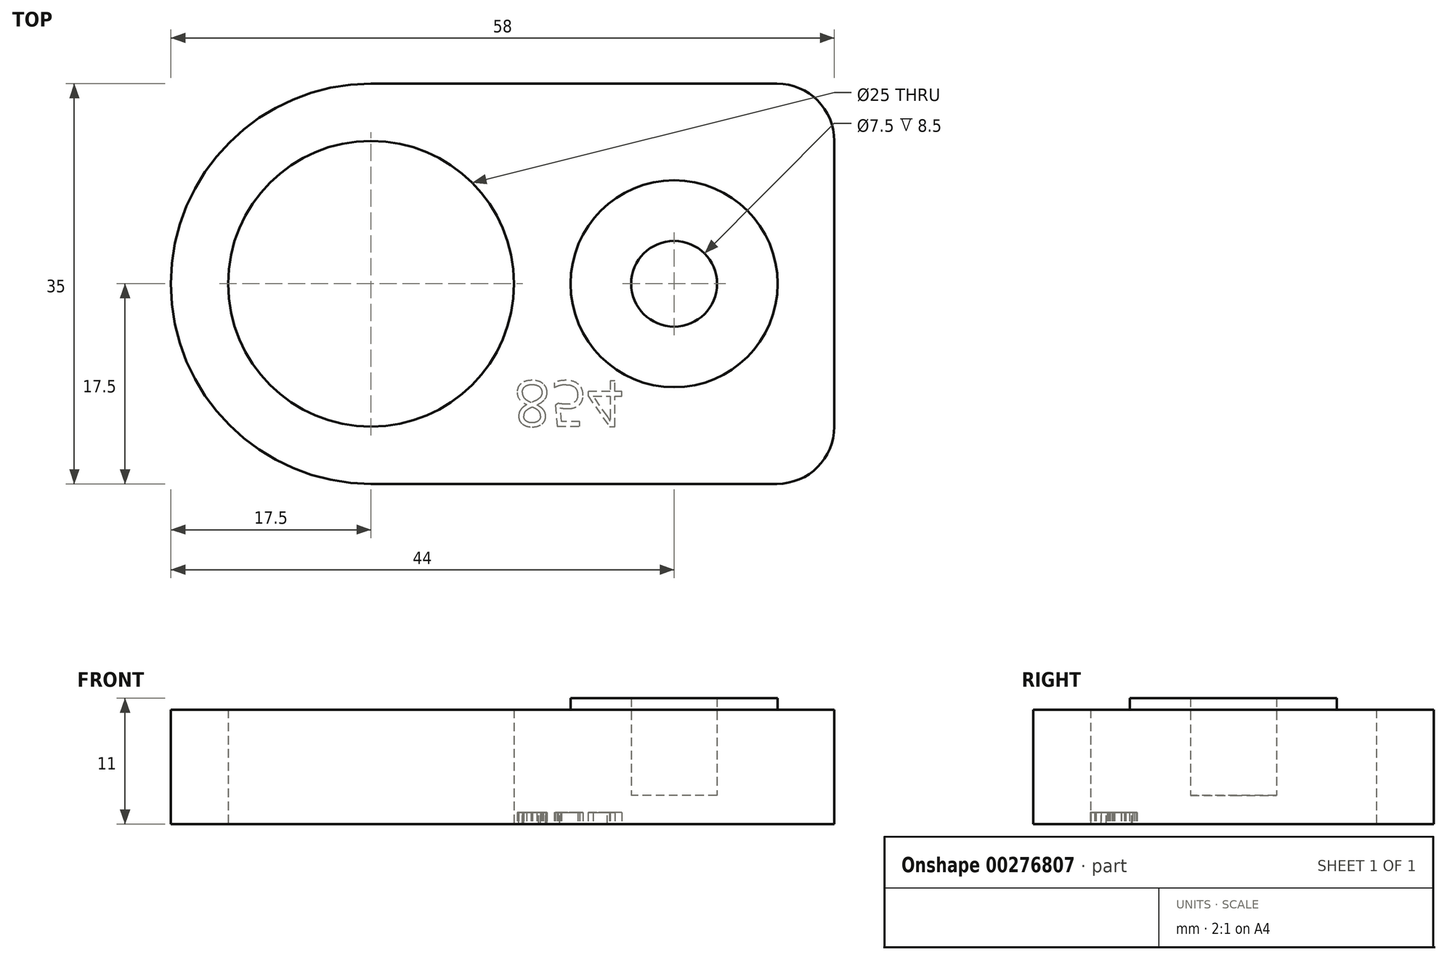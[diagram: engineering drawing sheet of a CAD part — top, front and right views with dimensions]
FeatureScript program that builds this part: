
annotation { "Feature Type Name" : "Feature", "Feature Type Description" : "" }
export const myFeature = defineFeature(function(context is Context, id is Id, definition is map)
    precondition{}
    {
        {
            var Q0;
            Q0=qCreatedBy(makeId("Top.planeOp"),FACE);
            var sketch = newSketch(context, id + "F0", { "sketchPlane" : qUnion([Q0])});
            skLineSegment(sketch, "E0.bottom", {"start": v(17.5, 0) * mm, "end": v(53, 0) * mm});
            skLineSegment(sketch, "E0.top", {"start": v(17.5, 35) * mm, "end": v(53, 35) * mm});
            skLineSegment(sketch, "E0.left", {"start": v(0, 17.5) * mm, "end": v(0, 17.5) * mm});
            skLineSegment(sketch, "E0.right", {"start": v(58, 5) * mm, "end": v(58, 30) * mm});
            skLineSegment(sketch, "E1.bottom", {"start": v(0, 0) * mm, "end": v(17.5, 0) * mm, "construction": true});
            skLineSegment(sketch, "E1.top", {"start": v(0, 17.5) * mm, "end": v(17.5, 17.5) * mm, "construction": true});
            skLineSegment(sketch, "E1.left", {"start": v(0, 0) * mm, "end": v(0, 17.5) * mm, "construction": true});
            skLineSegment(sketch, "E1.right", {"start": v(17.5, 0) * mm, "end": v(17.5, 17.5) * mm, "construction": true});
            skCircle(sketch, "E2", {"center": v(17.5, 17.5) * mm, "radius": 12.5 * mm});
            skPoint(sketch, "E3.visualSharp", {"position": v(0, 0) * mm});
            skArc(sketch, "E3.filletArc", {"start": v(0, 17.5) * mm, "mid": v(5.13, 5.13) * mm, "end": v(17.5, 0) * mm});
            skPoint(sketch, "E4.visualSharp", {"position": v(0, 35) * mm});
            skArc(sketch, "E4.filletArc", {"start": v(17.5, 35) * mm, "mid": v(5.13, 29.87) * mm, "end": v(0, 17.5) * mm});
            skPoint(sketch, "E5.visualSharp", {"position": v(58, 35) * mm});
            skArc(sketch, "E5.filletArc", {"start": v(58, 30) * mm, "mid": v(56.54, 33.54) * mm, "end": v(53, 35) * mm});
            skPoint(sketch, "E6.visualSharp", {"position": v(58, 0) * mm});
            skArc(sketch, "E6.filletArc", {"start": v(53, 0) * mm, "mid": v(56.54, 1.46) * mm, "end": v(58, 5) * mm});
            skSolve(sketch);
        }
        {
            var Q0;
            Q0=makeQuery(id+"F0.imprint","IMPRINT",FACE,{"disambiguationData":[TD([[makeQuery(id+"F0.imprint","IMPRINT",EDGE,{"derivedFrom":sQuery(id+"F0.wireOp",EDGE,"E0.bottom")}),1.0]])]});
            extrude(context, id + "F1", {"entities" : qUnion([Q0]), "depth" : 10 * mm});
        }
        {
            var Q0;
            Q0=makeQuery(id+"F1.opExtrude","CAP_FACE",FACE,{"disambiguationData":[OSD([sQuery(id+"F0.wireOp",EDGE,"E0.bottom"),sQuery(id+"F0.wireOp",EDGE,"E0.top"),sQuery(id+"F0.wireOp",EDGE,"E0.right"),sQuery(id+"F0.wireOp",EDGE,"E2"),sQuery(id+"F0.wireOp",EDGE,"E3.filletArc"),sQuery(id+"F0.wireOp",EDGE,"E4.filletArc"),sQuery(id+"F0.wireOp",EDGE,"E5.filletArc"),sQuery(id+"F0.wireOp",EDGE,"E6.filletArc")])],"isStart":false});
            var sketch = newSketch(context, id + "F2", { "sketchPlane" : qUnion([Q0])});
            skLineSegment(sketch, "E7.bottom", {"start": v(0, 0) * mm, "end": v(44, 0) * mm, "construction": true});
            skLineSegment(sketch, "E7.top", {"start": v(0, 17.5) * mm, "end": v(44, 17.5) * mm, "construction": true});
            skLineSegment(sketch, "E7.left", {"start": v(0, 0) * mm, "end": v(0, 17.5) * mm, "construction": true});
            skLineSegment(sketch, "E7.right", {"start": v(44, 0) * mm, "end": v(44, 17.5) * mm, "construction": true});
            skCircle(sketch, "E8", {"center": v(44, 17.5) * mm, "radius": 9.05 * mm});
            skCircle(sketch, "E9", {"center": v(44, 17.5) * mm, "radius": 3.75 * mm});
            skSolve(sketch);
        }
        {
            var Q0;
            Q0=makeQuery(id+"F2.imprint","IMPRINT",FACE,{"disambiguationData":[TD([[makeQuery(id+"F2.imprint","IMPRINT",EDGE,{"derivedFrom":sQuery(id+"F2.wireOp",EDGE,"E8")}),1.0]])]});
            extrude(context, id + "F3", {"entities" : qUnion([Q0]), "operationType" : NewBodyOperationType.ADD, "depth" : 1 * mm});
        }
        {
            var Q0;
            Q0=makeQuery(id+"F2.imprint","IMPRINT",FACE,{"disambiguationData":[TD([[makeQuery(id+"F2.imprint","IMPRINT",EDGE,{"derivedFrom":sQuery(id+"F2.wireOp",EDGE,"E9")}),1.0]])]});
            extrude(context, id + "F4", {"entities" : qUnion([Q0]), "operationType" : NewBodyOperationType.REMOVE, "oppositeDirection" : true, "depth" : 7.5 * mm});
        }
        {
            var Q0;
            Q0=makeQuery(id+"F1.opExtrude","CAP_FACE",FACE,{"disambiguationData":[OSD([sQuery(id+"F0.wireOp",EDGE,"E0.bottom"),sQuery(id+"F0.wireOp",EDGE,"E0.top"),sQuery(id+"F0.wireOp",EDGE,"E0.right"),sQuery(id+"F0.wireOp",EDGE,"E2"),sQuery(id+"F0.wireOp",EDGE,"E3.filletArc"),sQuery(id+"F0.wireOp",EDGE,"E4.filletArc"),sQuery(id+"F0.wireOp",EDGE,"E5.filletArc"),sQuery(id+"F0.wireOp",EDGE,"E6.filletArc")])],"isStart":true});
            var sketch = newSketch(context, id + "F5", { "sketchPlane" : qUnion([Q0])});
            skLineSegment(sketch, "E10.bottom", {"start": v(0, 0) * mm, "end": v(30, 0) * mm, "construction": true});
            skLineSegment(sketch, "E10.top", {"start": v(0, -5) * mm, "end": v(30, -5) * mm, "construction": true});
            skLineSegment(sketch, "E10.left", {"start": v(0, 0) * mm, "end": v(0, -5) * mm, "construction": true});
            skLineSegment(sketch, "E10.right", {"start": v(30, 0) * mm, "end": v(30, -5) * mm, "construction": true});
            skText(sketch, "E11", { "text": "854", "fontName": "OpenSans-Regular.ttf"});
            const initialGuessF5  = {"E11": [0.03, -0.009, 1, 0, 0.004]};
            skSetInitialGuess(sketch, initialGuessF5);
            skSolve(sketch);
        }
        {
            var Q0;
            Q0 = qSketchRegion(id + "F5", true);
            extrude(context, id + "F6", {"entities" : qUnion([Q0]), "operationType" : NewBodyOperationType.REMOVE, "oppositeDirection" : true, "depth" : 1 * mm});
        }
    });
